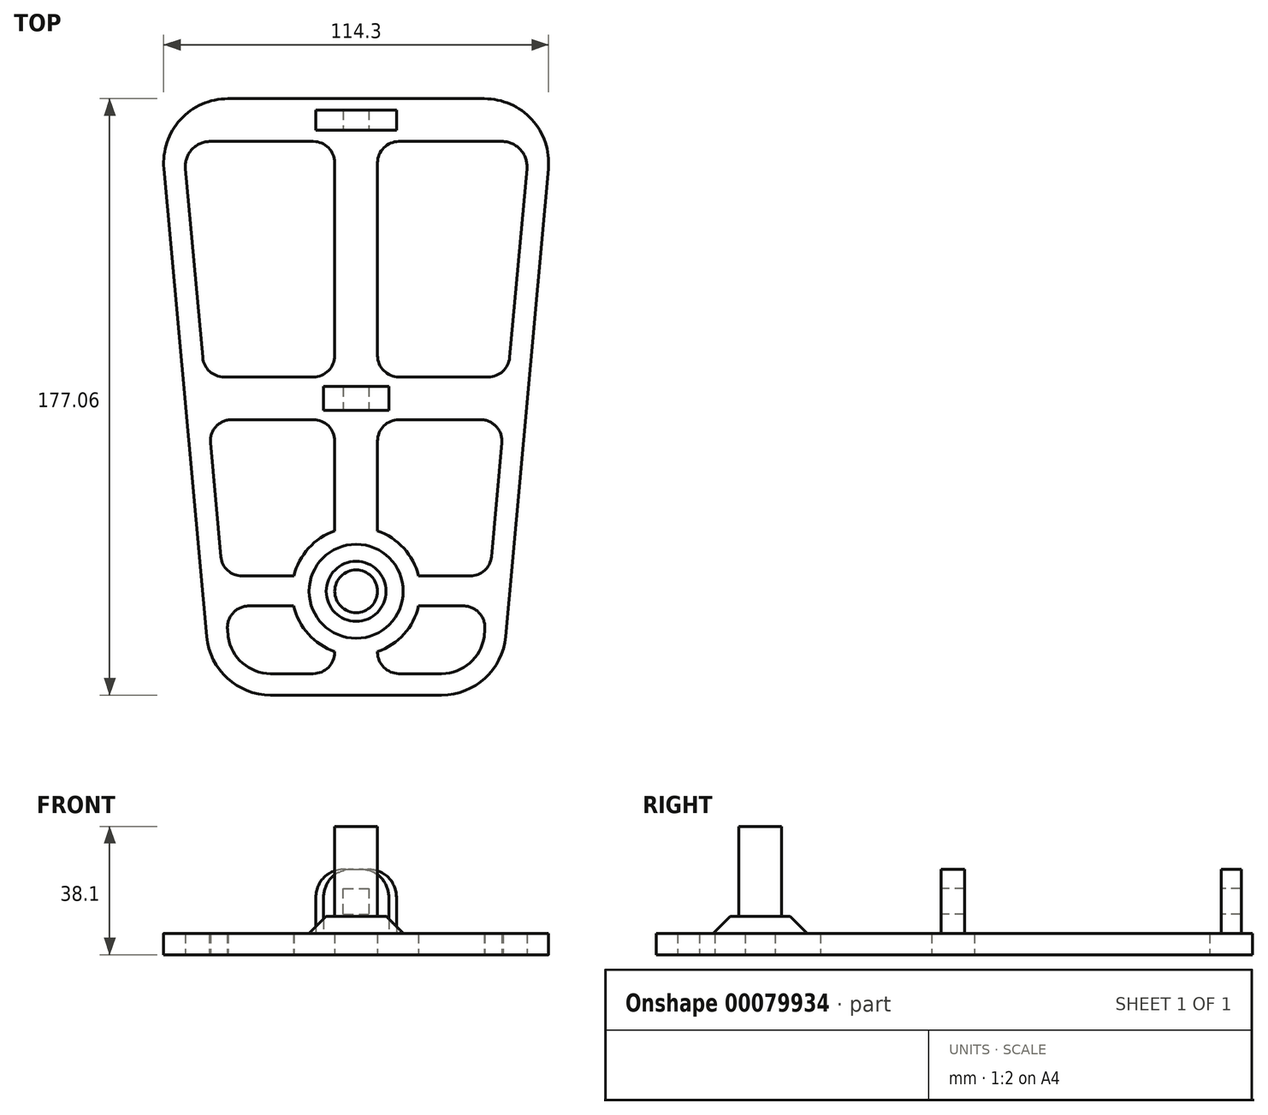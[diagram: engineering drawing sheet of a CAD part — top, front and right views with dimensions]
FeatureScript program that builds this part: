
annotation { "Feature Type Name" : "Feature", "Feature Type Description" : "" }
export const myFeature = defineFeature(function(context is Context, id is Id, definition is map)
    precondition{}
    {
        {
            var Q0;
            Q0=qCreatedBy(makeId("Top.planeOp"),FACE);
            var sketch = newSketch(context, id + "F0", { "sketchPlane" : qUnion([Q0])});
            skLineSegment(sketch, "E0", {"start": v(0, 88.96) * mm, "end": v(38.1, 88.96) * mm});
            skLineSegment(sketch, "E1", {"start": v(57.07, 68.17) * mm, "end": v(44.37, -70.79) * mm});
            skLineSegment(sketch, "E2", {"start": v(25.4, -88.1) * mm, "end": v(0, -88.1) * mm});
            skLineSegment(sketch, "E3.MirrorCS", {"start": v(0, 88.96) * mm, "end": v(-38.1, 88.96) * mm});
            skLineSegment(sketch, "E4.MirrorCS", {"start": v(-57.07, 68.17) * mm, "end": v(-44.37, -70.79) * mm});
            skLineSegment(sketch, "E5.MirrorCS", {"start": v(-25.4, -88.1) * mm, "end": v(0, -88.1) * mm});
            skPoint(sketch, "E6.visualSharp", {"position": v(-58.97, 88.96) * mm});
            skArc(sketch, "E6.filletArc", {"start": v(-38.1, 88.96) * mm, "mid": v(-52.17, 82.75) * mm, "end": v(-57.07, 68.17) * mm});
            skPoint(sketch, "E7.visualSharp", {"position": v(58.97, 88.96) * mm});
            skArc(sketch, "E7.filletArc", {"start": v(57.07, 68.17) * mm, "mid": v(52.17, 82.75) * mm, "end": v(38.1, 88.96) * mm});
            skPoint(sketch, "E8.visualSharp", {"position": v(-42.79, -88.1) * mm});
            skArc(sketch, "E8.filletArc", {"start": v(-44.37, -70.79) * mm, "mid": v(-38.24, -83.12) * mm, "end": v(-25.4, -88.1) * mm});
            skPoint(sketch, "E9.visualSharp", {"position": v(42.79, -88.1) * mm});
            skArc(sketch, "E9.filletArc", {"start": v(25.4, -88.1) * mm, "mid": v(38.24, -83.12) * mm, "end": v(44.37, -70.79) * mm});
            skArc(sketch, "E10.MirrorCS", {"start": v(-50.7, 68.17) * mm, "mid": v(-48.9, 73.72) * mm, "end": v(-43.66, 76.26) * mm});
            skArc(sketch, "E11.MirrorCS", {"start": v(-25.4, -81.75) * mm, "mid": v(-33.75, -78.63) * mm, "end": v(-38, -70.79) * mm});
            skLineSegment(sketch, "E12", {"start": v(-6.35, 69.9) * mm, "end": v(-6.35, 12.7) * mm});
            skLineSegment(sketch, "E13", {"start": v(-12.7, 6.35) * mm, "end": v(-39.25, 6.35) * mm});
            skLineSegment(sketch, "E14", {"start": v(-36.93, -6.35) * mm, "end": v(-12.7, -6.35) * mm});
            skLineSegment(sketch, "E15", {"start": v(-12.7, 76.26) * mm, "end": v(-43.66, 76.26) * mm});
            skLineSegment(sketch, "E16", {"start": v(-50.7, 68.17) * mm, "end": v(-45.57, 12.12) * mm});
            skLineSegment(sketch, "E17", {"start": v(-12.7, -81.75) * mm, "end": v(-25.4, -81.75) * mm});
            skLineSegment(sketch, "E18.MirrorCS", {"start": v(6.35, 69.9) * mm, "end": v(6.35, 12.7) * mm});
            skLineSegment(sketch, "E19.MirrorCS", {"start": v(12.7, 76.26) * mm, "end": v(43.66, 76.26) * mm});
            skArc(sketch, "E20.MirrorCS", {"start": v(50.7, 68.17) * mm, "mid": v(48.9, 73.72) * mm, "end": v(43.66, 76.26) * mm});
            skLineSegment(sketch, "E21.MirrorCS", {"start": v(50.7, 68.17) * mm, "end": v(45.57, 12.12) * mm});
            skLineSegment(sketch, "E22.MirrorCS", {"start": v(12.7, 6.35) * mm, "end": v(39.25, 6.35) * mm});
            skLineSegment(sketch, "E23.MirrorCS", {"start": v(36.93, -6.35) * mm, "end": v(12.7, -6.35) * mm});
            skArc(sketch, "E24.MirrorCS", {"start": v(25.4, -81.75) * mm, "mid": v(33.75, -78.63) * mm, "end": v(38, -70.79) * mm});
            skLineSegment(sketch, "E25.MirrorCS", {"start": v(12.7, -81.75) * mm, "end": v(25.4, -81.75) * mm});
            skLineSegment(sketch, "E26", {"start": v(-6.35, -61.67) * mm, "end": v(-31.87, -61.67) * mm});
            skLineSegment(sketch, "E27", {"start": v(-6.35, -52.78) * mm, "end": v(-33.84, -52.78) * mm});
            skLineSegment(sketch, "E28.MirrorCS", {"start": v(6.35, -52.78) * mm, "end": v(33.84, -52.78) * mm});
            skLineSegment(sketch, "E29.MirrorCS", {"start": v(6.35, -61.67) * mm, "end": v(31.87, -61.67) * mm});
            skLineSegment(sketch, "E30", {"start": v(-43.25, -13.28) * mm, "end": v(-40.17, -47) * mm});
            skLineSegment(sketch, "E31", {"start": v(-38.2, -68.6) * mm, "end": v(-38, -70.79) * mm});
            skLineSegment(sketch, "E32", {"start": v(-6.35, -61.67) * mm, "end": v(-6.35, -75.4) * mm});
            skLineSegment(sketch, "E33", {"start": v(-6.35, -52.78) * mm, "end": v(-6.35, -12.7) * mm});
            skLineSegment(sketch, "E34.MirrorCS", {"start": v(6.35, -52.78) * mm, "end": v(6.35, -12.7) * mm});
            skLineSegment(sketch, "E35.MirrorCS", {"start": v(43.25, -13.28) * mm, "end": v(40.17, -47) * mm});
            skLineSegment(sketch, "E36.MirrorCS", {"start": v(6.35, -61.67) * mm, "end": v(6.35, -75.4) * mm});
            skLineSegment(sketch, "E37.MirrorCS", {"start": v(38.2, -68.6) * mm, "end": v(38, -70.79) * mm});
            skPoint(sketch, "E38.visualSharp", {"position": v(-6.35, 76.26) * mm});
            skArc(sketch, "E38.filletArc", {"start": v(-6.35, 69.9) * mm, "mid": v(-8.2, 74.4) * mm, "end": v(-12.7, 76.26) * mm});
            skPoint(sketch, "E39.visualSharp", {"position": v(6.35, 76.26) * mm});
            skArc(sketch, "E39.filletArc", {"start": v(12.7, 76.26) * mm, "mid": v(8.2, 74.4) * mm, "end": v(6.35, 69.9) * mm});
            skPoint(sketch, "E40.visualSharp", {"position": v(45.04, 6.35) * mm});
            skArc(sketch, "E40.filletArc", {"start": v(39.25, 6.35) * mm, "mid": v(43.53, 8) * mm, "end": v(45.57, 12.12) * mm});
            skPoint(sketch, "E41.visualSharp", {"position": v(6.35, 6.35) * mm});
            skArc(sketch, "E41.filletArc", {"start": v(6.35, 12.7) * mm, "mid": v(8.2, 8.2) * mm, "end": v(12.7, 6.35) * mm});
            skPoint(sketch, "E42.visualSharp", {"position": v(-6.35, 6.35) * mm});
            skArc(sketch, "E42.filletArc", {"start": v(-12.7, 6.35) * mm, "mid": v(-8.2, 8.2) * mm, "end": v(-6.35, 12.7) * mm});
            skPoint(sketch, "E43.visualSharp", {"position": v(-45.04, 6.35) * mm});
            skArc(sketch, "E43.filletArc", {"start": v(-45.57, 12.12) * mm, "mid": v(-43.53, 8) * mm, "end": v(-39.25, 6.35) * mm});
            skCircle(sketch, "E44", {"center": v(0, -57.3) * mm, "radius": 19.05 * mm});
            skCircle(sketch, "E45", {"center": v(0, -57.3) * mm, "radius": 13.97 * mm});
            skCircle(sketch, "E46", {"center": v(0, -57.3) * mm, "radius": 6.35 * mm});
            skLineSegment(sketch, "E47", {"start": v(0, 85.6) * mm, "end": v(11.99, 85.6) * mm});
            skLineSegment(sketch, "E48", {"start": v(11.99, 85.6) * mm, "end": v(11.99, 79.58) * mm});
            skLineSegment(sketch, "E49", {"start": v(11.99, 79.58) * mm, "end": v(0, 79.58) * mm});
            skLineSegment(sketch, "E50", {"start": v(0, 3.48) * mm, "end": v(9.73, 3.48) * mm});
            skLineSegment(sketch, "E51", {"start": v(9.73, 3.48) * mm, "end": v(9.73, -3.56) * mm});
            skLineSegment(sketch, "E52", {"start": v(9.73, -3.56) * mm, "end": v(0, -3.56) * mm});
            skLineSegment(sketch, "E53.MirrorCS", {"start": v(-11.99, 79.58) * mm, "end": v(0, 79.58) * mm});
            skLineSegment(sketch, "E54.MirrorCS", {"start": v(0, 85.6) * mm, "end": v(-11.99, 85.6) * mm});
            skLineSegment(sketch, "E55.MirrorCS", {"start": v(-11.99, 85.6) * mm, "end": v(-11.99, 79.58) * mm});
            skLineSegment(sketch, "E56.MirrorCS", {"start": v(0, 3.48) * mm, "end": v(-9.73, 3.48) * mm});
            skLineSegment(sketch, "E57.MirrorCS", {"start": v(-9.73, -3.56) * mm, "end": v(0, -3.56) * mm});
            skLineSegment(sketch, "E58.MirrorCS", {"start": v(-9.73, 3.48) * mm, "end": v(-9.73, -3.56) * mm});
            skPoint(sketch, "E59.visualSharp", {"position": v(-43.88, -6.35) * mm});
            skArc(sketch, "E59.filletArc", {"start": v(-36.93, -6.35) * mm, "mid": v(-41.62, -8.42) * mm, "end": v(-43.25, -13.28) * mm});
            skPoint(sketch, "E60.visualSharp", {"position": v(43.88, -6.35) * mm});
            skArc(sketch, "E60.filletArc", {"start": v(43.25, -13.28) * mm, "mid": v(41.62, -8.42) * mm, "end": v(36.93, -6.35) * mm});
            skPoint(sketch, "E61.visualSharp", {"position": v(6.35, -6.35) * mm});
            skArc(sketch, "E61.filletArc", {"start": v(12.7, -6.35) * mm, "mid": v(8.2, -8.2) * mm, "end": v(6.35, -12.7) * mm});
            skPoint(sketch, "E62.visualSharp", {"position": v(-6.35, -6.35) * mm});
            skArc(sketch, "E62.filletArc", {"start": v(-6.35, -12.7) * mm, "mid": v(-8.2, -8.2) * mm, "end": v(-12.7, -6.35) * mm});
            skPoint(sketch, "E63.visualSharp", {"position": v(-39.64, -52.78) * mm});
            skArc(sketch, "E63.filletArc", {"start": v(-40.17, -47) * mm, "mid": v(-38.12, -51.12) * mm, "end": v(-33.84, -52.78) * mm});
            skPoint(sketch, "E64.visualSharp", {"position": v(39.64, -52.78) * mm});
            skArc(sketch, "E64.filletArc", {"start": v(33.84, -52.78) * mm, "mid": v(38.12, -51.12) * mm, "end": v(40.17, -47) * mm});
            skPoint(sketch, "E65.visualSharp", {"position": v(38.83, -61.67) * mm});
            skArc(sketch, "E65.filletArc", {"start": v(38.2, -68.6) * mm, "mid": v(36.56, -63.74) * mm, "end": v(31.87, -61.67) * mm});
            skPoint(sketch, "E66.visualSharp", {"position": v(6.35, -81.75) * mm});
            skArc(sketch, "E66.filletArc", {"start": v(6.35, -75.4) * mm, "mid": v(8.2, -79.9) * mm, "end": v(12.7, -81.75) * mm});
            skPoint(sketch, "E67.visualSharp", {"position": v(-6.35, -81.75) * mm});
            skArc(sketch, "E67.filletArc", {"start": v(-12.7, -81.75) * mm, "mid": v(-8.2, -79.9) * mm, "end": v(-6.35, -75.4) * mm});
            skPoint(sketch, "E68.visualSharp", {"position": v(-38.83, -61.67) * mm});
            skArc(sketch, "E68.filletArc", {"start": v(-31.87, -61.67) * mm, "mid": v(-36.56, -63.74) * mm, "end": v(-38.2, -68.6) * mm});
            skSolve(sketch);
        }
        {
            var Q0;
            Q0=makeQuery(id+"F0.imprint","IMPRINT",FACE,{"disambiguationData":[TD([[makeQuery(id+"F0.imprint","IMPRINT",EDGE,{"derivedFrom":sQuery(id+"F0.wireOp",EDGE,"E0")}),-1.0]])]});
            var Q1;
            {var subQ0=sQuery(id+"F0.wireOp",EDGE,"E45");var subQ1=sQuery(id+"F0.wireOp",EDGE,"E32");var subQ2=makeQuery(id+"F0.imprint","INTERSECT",VERTEX,{"derivedFrom":[subQ1,subQ0]});Q1=makeQuery(id+"F0.imprint","IMPRINT",FACE,{"disambiguationData":[TD([[makeQuery(id+"F0.imprint","IMPRINT",EDGE,{"disambiguationData":[TD([[subQ2,-1.0]])],"derivedFrom":subQ1}),1.0]])]});}
            var Q2;
            {var subQ0=sQuery(id+"F0.wireOp",EDGE,"E45");var subQ1=sQuery(id+"F0.wireOp",EDGE,"E29.MirrorCS");var subQ2=makeQuery(id+"F0.imprint","INTERSECT",VERTEX,{"derivedFrom":[subQ1,subQ0]});Q2=makeQuery(id+"F0.imprint","IMPRINT",FACE,{"disambiguationData":[TD([[makeQuery(id+"F0.imprint","IMPRINT",EDGE,{"disambiguationData":[TD([[subQ2,-1.0]])],"derivedFrom":subQ1}),-1.0]])]});}
            var Q3;
            {var subQ0=sQuery(id+"F0.wireOp",EDGE,"E45");var subQ1=sQuery(id+"F0.wireOp",EDGE,"E28.MirrorCS");var subQ2=makeQuery(id+"F0.imprint","INTERSECT",VERTEX,{"derivedFrom":[subQ1,subQ0]});Q3=makeQuery(id+"F0.imprint","IMPRINT",FACE,{"disambiguationData":[TD([[makeQuery(id+"F0.imprint","IMPRINT",EDGE,{"disambiguationData":[TD([[subQ2,-1.0]])],"derivedFrom":subQ1}),-1.0]])]});}
            var Q4;
            {var subQ0=sQuery(id+"F0.wireOp",EDGE,"E45");var subQ1=sQuery(id+"F0.wireOp",EDGE,"E28.MirrorCS");var subQ2=makeQuery(id+"F0.imprint","INTERSECT",VERTEX,{"derivedFrom":[subQ1,subQ0]});Q4=makeQuery(id+"F0.imprint","IMPRINT",FACE,{"disambiguationData":[TD([[makeQuery(id+"F0.imprint","IMPRINT",EDGE,{"disambiguationData":[TD([[subQ2,-1.0]])],"derivedFrom":subQ1}),1.0]])]});}
            var Q5;
            {var subQ0=sQuery(id+"F0.wireOp",EDGE,"E45");var subQ1=sQuery(id+"F0.wireOp",EDGE,"E27");var subQ2=makeQuery(id+"F0.imprint","INTERSECT",VERTEX,{"derivedFrom":[subQ1,subQ0]});Q5=makeQuery(id+"F0.imprint","IMPRINT",FACE,{"disambiguationData":[TD([[makeQuery(id+"F0.imprint","IMPRINT",EDGE,{"disambiguationData":[TD([[subQ2,-1.0]])],"derivedFrom":subQ1}),-1.0]])]});}
            var Q6;
            {var subQ0=sQuery(id+"F0.wireOp",EDGE,"E45");var subQ1=sQuery(id+"F0.wireOp",EDGE,"E26");var subQ2=makeQuery(id+"F0.imprint","INTERSECT",VERTEX,{"derivedFrom":[subQ1,subQ0]});Q6=makeQuery(id+"F0.imprint","IMPRINT",FACE,{"disambiguationData":[TD([[makeQuery(id+"F0.imprint","IMPRINT",EDGE,{"disambiguationData":[TD([[subQ2,-1.0]])],"derivedFrom":subQ1}),1.0]])]});}
            var Q7;
            {var subQ0=sQuery(id+"F0.wireOp",EDGE,"E45");var subQ1=sQuery(id+"F0.wireOp",EDGE,"E26");var subQ2=makeQuery(id+"F0.imprint","INTERSECT",VERTEX,{"derivedFrom":[subQ1,subQ0]});Q7=makeQuery(id+"F0.imprint","IMPRINT",FACE,{"disambiguationData":[TD([[makeQuery(id+"F0.imprint","IMPRINT",EDGE,{"disambiguationData":[TD([[subQ2,-1.0]])],"derivedFrom":subQ1}),-1.0]])]});}
            var Q8;
            {var subQ0=sQuery(id+"F0.wireOp",EDGE,"E45");var subQ1=sQuery(id+"F0.wireOp",EDGE,"E33");var subQ2=makeQuery(id+"F0.imprint","INTERSECT",VERTEX,{"derivedFrom":[subQ1,subQ0]});Q8=makeQuery(id+"F0.imprint","IMPRINT",FACE,{"disambiguationData":[TD([[makeQuery(id+"F0.imprint","IMPRINT",EDGE,{"disambiguationData":[TD([[subQ2,-1.0]])],"derivedFrom":subQ1}),-1.0]])]});}
            extrude(context, id + "F1", {"entities" : qUnion([Q0, Q1, Q2, Q3, Q4, Q5, Q6, Q7, Q8]), "depth" : 6.35 * mm});
        }
        {
            var Q0;
            Q0=makeQuery(id+"F0.imprint","IMPRINT",FACE,{"disambiguationData":[TD([[makeQuery(id+"F0.imprint","IMPRINT",EDGE,{"derivedFrom":sQuery(id+"F0.wireOp",EDGE,"E50")}),-1.0]])]});
            var Q1;
            Q1=makeQuery(id+"F0.imprint","IMPRINT",FACE,{"disambiguationData":[TD([[makeQuery(id+"F0.imprint","IMPRINT",EDGE,{"derivedFrom":sQuery(id+"F0.wireOp",EDGE,"E47")}),-1.0]])]});
            extrude(context, id + "F2", {"entities" : qUnion([Q0, Q1]), "operationType" : NewBodyOperationType.ADD, "depth" : 25.4 * mm});
        }
        {
            var Q0;
            Q0=makeQuery(id+"F2.opExtrude","CAP_EDGE",EDGE,{"disambiguationData":[OSD([sQuery(id+"F0.wireOp",EDGE,"E58.MirrorCS")])],"isStart":false});
            var Q1;
            Q1=makeQuery(id+"F2.opExtrude","CAP_EDGE",EDGE,{"disambiguationData":[OSD([sQuery(id+"F0.wireOp",EDGE,"E51")])],"isStart":false});
            var Q2;
            Q2=makeQuery(id+"F2.opExtrude","CAP_EDGE",EDGE,{"disambiguationData":[OSD([sQuery(id+"F0.wireOp",EDGE,"E48")])],"isStart":false});
            var Q3;
            Q3=makeQuery(id+"F2.opExtrude","CAP_EDGE",EDGE,{"disambiguationData":[OSD([sQuery(id+"F0.wireOp",EDGE,"E55.MirrorCS")])],"isStart":false});
            fillet(context, id + "F3", {"entities" : qUnion([Q0, Q1, Q2, Q3]), "radius" : 8.9 * mm, "rho" : 0.45, "crossSection" : FilletCrossSection.CONIC, "allowEdgeOverflow" : false});
        }
        {
            var Q0;
            Q0=makeQuery(id+"F2.opExtrude","SWEPT_FACE",FACE,{"disambiguationData":[OSD([sQuery(id+"F0.wireOp",EDGE,"E52"),sQuery(id+"F0.wireOp",EDGE,"E57.MirrorCS")])]});
            var sketch = newSketch(context, id + "F4", { "sketchPlane" : qUnion([Q0])});
            skPoint(sketch, "E69", {"position": v(0, 15.88) * mm});
            skPoint(sketch, "E70", {"position": v(0, 25.4) * mm});
            skPoint(sketch, "E71", {"position": v(0, 6.35) * mm});
            skLineSegment(sketch, "E72", {"start": v(0, 19.69) * mm, "end": v(3.8, 19.69) * mm});
            skLineSegment(sketch, "E73", {"start": v(3.8, 19.69) * mm, "end": v(3.8, 15.88) * mm});
            skLineSegment(sketch, "E74.MirrorCS", {"start": v(0, 19.69) * mm, "end": v(-3.8, 19.69) * mm});
            skLineSegment(sketch, "E75.MirrorCS", {"start": v(-3.8, 19.69) * mm, "end": v(-3.8, 15.88) * mm});
            skLineSegment(sketch, "E76.MirrorCS", {"start": v(0, 12.06) * mm, "end": v(3.8, 12.06) * mm});
            skLineSegment(sketch, "E77.MirrorCS", {"start": v(0, 12.06) * mm, "end": v(-3.8, 12.06) * mm});
            skLineSegment(sketch, "E78.MirrorCS", {"start": v(-3.8, 12.06) * mm, "end": v(-3.8, 15.88) * mm});
            skLineSegment(sketch, "E79.MirrorCS", {"start": v(3.8, 12.06) * mm, "end": v(3.8, 15.88) * mm});
            skSolve(sketch);
        }
        {
            var Q0;
            Q0=makeQuery(id+"F4.imprint","IMPRINT",FACE,{"disambiguationData":[TD([[makeQuery(id+"F4.imprint","IMPRINT",EDGE,{"derivedFrom":sQuery(id+"F4.wireOp",EDGE,"E72")}),-1.0]])]});
            extrude(context, id + "F5", {"entities" : qUnion([Q0]), "operationType" : NewBodyOperationType.REMOVE, "endBound" : BoundingType.THROUGH_ALL, "oppositeDirection" : true, "depth" : 25.4 * mm});
        }
        {
            var Q0;
            Q0=makeQuery(id+"F0.imprint","IMPRINT",FACE,{"disambiguationData":[TD([[makeQuery(id+"F0.imprint","IMPRINT",EDGE,{"derivedFrom":sQuery(id+"F0.wireOp",EDGE,"E46")}),-1.0]])]});
            var Q1;
            {var subQ0=sQuery(id+"F0.wireOp",EDGE,"E33");var subQ1=sQuery(id+"F0.wireOp",EDGE,"E27");var subQ2=makeQuery(id+"F0.imprint","INTERSECT",VERTEX,{"derivedFrom":[subQ1,subQ0]});Q1=makeQuery(id+"F0.imprint","IMPRINT",FACE,{"disambiguationData":[TD([[makeQuery(id+"F0.imprint","IMPRINT",EDGE,{"disambiguationData":[TD([[subQ2,-1.0]])],"derivedFrom":subQ1}),-1.0]])]});}
            var Q2;
            {var subQ0=sQuery(id+"F0.wireOp",EDGE,"E32");var subQ1=sQuery(id+"F0.wireOp",EDGE,"E26");var subQ2=makeQuery(id+"F0.imprint","INTERSECT",VERTEX,{"derivedFrom":[subQ1,subQ0]});Q2=makeQuery(id+"F0.imprint","IMPRINT",FACE,{"disambiguationData":[TD([[makeQuery(id+"F0.imprint","IMPRINT",EDGE,{"disambiguationData":[TD([[subQ2,-1.0]])],"derivedFrom":subQ1}),1.0]])]});}
            var Q3;
            {var subQ0=sQuery(id+"F0.wireOp",EDGE,"E34.MirrorCS");var subQ1=sQuery(id+"F0.wireOp",EDGE,"E28.MirrorCS");var subQ2=makeQuery(id+"F0.imprint","INTERSECT",VERTEX,{"derivedFrom":[subQ1,subQ0]});Q3=makeQuery(id+"F0.imprint","IMPRINT",FACE,{"disambiguationData":[TD([[makeQuery(id+"F0.imprint","IMPRINT",EDGE,{"disambiguationData":[TD([[subQ2,-1.0]])],"derivedFrom":subQ1}),1.0]])]});}
            var Q4;
            {var subQ0=sQuery(id+"F0.wireOp",EDGE,"E36.MirrorCS");var subQ1=sQuery(id+"F0.wireOp",EDGE,"E29.MirrorCS");var subQ2=makeQuery(id+"F0.imprint","INTERSECT",VERTEX,{"derivedFrom":[subQ1,subQ0]});Q4=makeQuery(id+"F0.imprint","IMPRINT",FACE,{"disambiguationData":[TD([[makeQuery(id+"F0.imprint","IMPRINT",EDGE,{"disambiguationData":[TD([[subQ2,-1.0]])],"derivedFrom":subQ1}),-1.0]])]});}
            extrude(context, id + "F6", {"entities" : qUnion([Q0, Q1, Q2, Q3, Q4]), "operationType" : NewBodyOperationType.ADD, "depth" : 11.43 * mm});
        }
        {
            var Q0;
            Q0=makeQuery(id+"F6.opExtrude","CAP_EDGE",EDGE,{"disambiguationData":[OSD([sQuery(id+"F0.wireOp",EDGE,"E45")])],"isStart":false});
            chamfer(context, id + "F7", {"entities" : qUnion([Q0]), "width" : 5.08 * mm, "tangentPropagation" : true});
        }
        {
            var Q0;
            Q0=makeQuery(id+"F0.imprint","IMPRINT",FACE,{"disambiguationData":[TD([[makeQuery(id+"F0.imprint","IMPRINT",EDGE,{"derivedFrom":sQuery(id+"F0.wireOp",EDGE,"E46")}),1.0]])]});
            extrude(context, id + "F8", {"entities" : qUnion([Q0]), "operationType" : NewBodyOperationType.ADD, "depth" : 38.1 * mm});
        }
    });
